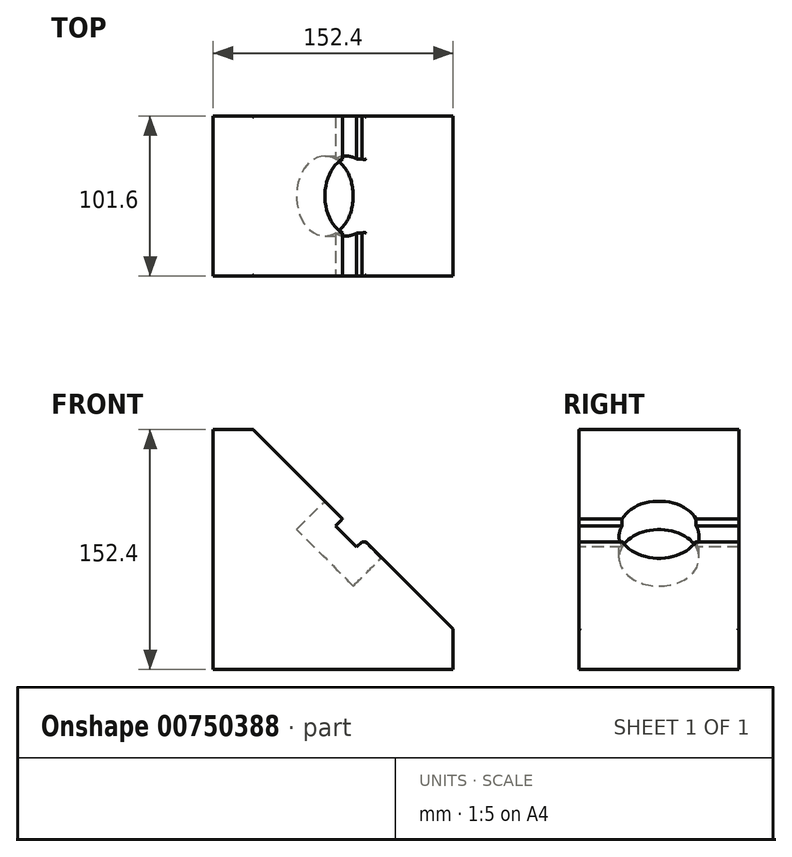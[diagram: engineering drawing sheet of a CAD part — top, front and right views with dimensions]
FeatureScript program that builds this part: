
annotation { "Feature Type Name" : "Feature", "Feature Type Description" : "" }
export const myFeature = defineFeature(function(context is Context, id is Id, definition is map)
    precondition{}
    {
        {
            var Q0;
            Q0=qCreatedBy(makeId("Front.planeOp"),FACE);
            var sketch = newSketch(context, id + "F0", { "sketchPlane" : qUnion([Q0])});
            skLineSegment(sketch, "E0", {"start": v(0, 0) * mm, "end": v(152.4, 0) * mm});
            skLineSegment(sketch, "E1", {"start": v(0, 0) * mm, "end": v(0, 152.4) * mm});
            skLineSegment(sketch, "E2", {"start": v(152.4, 0) * mm, "end": v(152.4, 25.4) * mm});
            skLineSegment(sketch, "E3", {"start": v(0, 152.4) * mm, "end": v(25.4, 152.4) * mm});
            skLineSegment(sketch, "E4", {"start": v(25.4, 152.4) * mm, "end": v(152.4, 25.4) * mm});
            skSolve(sketch);
        }
        {
            var Q0;
            Q0=makeQuery(id+"F0.imprint","IMPRINT",FACE,{"disambiguationData":[TD([[makeQuery(id+"F0.imprint","IMPRINT",EDGE,{"derivedFrom":sQuery(id+"F0.wireOp",EDGE,"E0")}),1.0]])]});
            extrude(context, id + "F1", {"entities" : qUnion([Q0]), "depth" : 50.8 * mm, "offsetDistance" : 25.4 * mm, "hasSecondDirection" : true, "secondDirectionOppositeDirection" : true, "secondDirectionDepth" : 50.8 * mm});
        }
        {
            var Q0;
            Q0=makeQuery(id+"F1.opExtrude","SWEPT_FACE",FACE,{"disambiguationData":[OSD([sQuery(id+"F0.wireOp",EDGE,"E4")])]});
            var sketch = newSketch(context, id + "F2", { "sketchPlane" : qUnion([Q0])});
            skCircle(sketch, "E5", {"center": v(0, 0) * mm, "radius": 25.4 * mm});
            skSolve(sketch);
        }
        {
            var Q0;
            Q0=makeQuery(id+"F2.imprint","IMPRINT",FACE,{"disambiguationData":[TD([[makeQuery(id+"F2.imprint","IMPRINT",EDGE,{"derivedFrom":sQuery(id+"F2.wireOp",EDGE,"E5")}),1.0]])]});
            var Q1;
            Q1=sQuery(id+"F2.wireOp",EDGE,"E5");
            extrude(context, id + "F3", {"entities" : qUnion([Q0]), "operationType" : NewBodyOperationType.REMOVE, "surfaceEntities" : qUnion([Q1]), "oppositeDirection" : true, "depth" : 25.4 * mm, "offsetDistance" : 25.4 * mm});
        }
        {
            var Q0;
            Q0=makeQuery(id+"F1.opExtrude","SWEPT_FACE",FACE,{"disambiguationData":[OSD([sQuery(id+"F0.wireOp",EDGE,"E4")])]});
            var sketch = newSketch(context, id + "F4", { "sketchPlane" : qUnion([Q0])});
            skPoint(sketch, "E6.middle", {"position": v(0, 0) * mm});
            skLineSegment(sketch, "E7.bottom", {"start": v(55.28, 9.53) * mm, "end": v(-55.28, 9.53) * mm});
            skLineSegment(sketch, "E7.top", {"start": v(55.28, -9.53) * mm, "end": v(-55.28, -9.53) * mm});
            skLineSegment(sketch, "E7.left", {"start": v(55.28, 9.53) * mm, "end": v(55.28, -9.53) * mm});
            skLineSegment(sketch, "E7.right", {"start": v(-55.28, 9.53) * mm, "end": v(-55.28, -9.53) * mm});
            skSolve(sketch);
        }
        {
            var Q0;
            Q0 = qSketchRegion(id + "F4", true);
            extrude(context, id + "F5", {"entities" : qUnion([Q0]), "operationType" : NewBodyOperationType.REMOVE, "oppositeDirection" : true, "depth" : 6.35 * mm, "offsetDistance" : 25.4 * mm});
        }
        {
            var Q0;
            {var subQ0=sQuery(id+"F0.wireOp",EDGE,"E4");var subQ1=sQuery(id+"F4.wireOp",EDGE,"E7.bottom");Q0=makeQuery(id+"F5.boolean.opBoolean","COPY",EDGE,{"disambiguationData":[TD([makeQuery(id+"F1.opExtrude","CAP_FACE",FACE,{"disambiguationData":[OSD([sQuery(id+"F0.wireOp",EDGE,"E0"),sQuery(id+"F0.wireOp",EDGE,"E1"),sQuery(id+"F0.wireOp",EDGE,"E2"),sQuery(id+"F0.wireOp",EDGE,"E3"),subQ0])],"isStart":false})])],"derivedFrom":makeQuery(id+"F5.opExtrude","CAP_EDGE",EDGE,{"disambiguationData":[OSD([subQ1])],"isStart":true})});}
            var Q1;
            {var subQ0=sQuery(id+"F0.wireOp",EDGE,"E4");var subQ1=sQuery(id+"F4.wireOp",EDGE,"E7.top");Q1=makeQuery(id+"F5.boolean.opBoolean","COPY",EDGE,{"disambiguationData":[TD([makeQuery(id+"F1.opExtrude","CAP_FACE",FACE,{"disambiguationData":[OSD([sQuery(id+"F0.wireOp",EDGE,"E0"),sQuery(id+"F0.wireOp",EDGE,"E1"),sQuery(id+"F0.wireOp",EDGE,"E2"),sQuery(id+"F0.wireOp",EDGE,"E3"),subQ0])],"isStart":false})])],"derivedFrom":makeQuery(id+"F5.opExtrude","CAP_EDGE",EDGE,{"disambiguationData":[OSD([subQ1])],"isStart":true})});}
            var Q2;
            {var subQ0=sQuery(id+"F0.wireOp",EDGE,"E4");var subQ1=sQuery(id+"F4.wireOp",EDGE,"E7.top");Q2=makeQuery(id+"F5.boolean.opBoolean","COPY",EDGE,{"disambiguationData":[TD([makeQuery(id+"F1.opExtrude","CAP_FACE",FACE,{"disambiguationData":[OSD([sQuery(id+"F0.wireOp",EDGE,"E0"),sQuery(id+"F0.wireOp",EDGE,"E1"),sQuery(id+"F0.wireOp",EDGE,"E2"),sQuery(id+"F0.wireOp",EDGE,"E3"),subQ0])],"isStart":true})])],"derivedFrom":makeQuery(id+"F5.opExtrude","CAP_EDGE",EDGE,{"disambiguationData":[OSD([subQ1])],"isStart":true})});}
            var Q3;
            {var subQ0=sQuery(id+"F0.wireOp",EDGE,"E4");var subQ1=sQuery(id+"F4.wireOp",EDGE,"E7.bottom");Q3=makeQuery(id+"F5.boolean.opBoolean","COPY",EDGE,{"disambiguationData":[TD([makeQuery(id+"F1.opExtrude","CAP_FACE",FACE,{"disambiguationData":[OSD([sQuery(id+"F0.wireOp",EDGE,"E0"),sQuery(id+"F0.wireOp",EDGE,"E1"),sQuery(id+"F0.wireOp",EDGE,"E2"),sQuery(id+"F0.wireOp",EDGE,"E3"),subQ0])],"isStart":true})])],"derivedFrom":makeQuery(id+"F5.opExtrude","CAP_EDGE",EDGE,{"disambiguationData":[OSD([subQ1])],"isStart":true})});}
            var Q4;
            {var subQ0=sQuery(id+"F2.wireOp",EDGE,"E5");Q4=makeQuery(id+"F5.boolean.opBoolean","SPLIT",EDGE,{"disambiguationData":[TD([makeQuery(id+"F5.opExtrude","SWEPT_FACE",FACE,{"disambiguationData":[OSD([sQuery(id+"F4.wireOp",EDGE,"E7.bottom")])]})])],"derivedFrom":makeQuery(id+"F3.boolean.opBoolean","COPY",EDGE,{"derivedFrom":makeQuery(id+"F3.opExtrude","CAP_EDGE",EDGE,{"disambiguationData":[OSD([subQ0])],"isStart":true})})});}
            var Q5;
            {var subQ0=sQuery(id+"F2.wireOp",EDGE,"E5");Q5=makeQuery(id+"F5.boolean.opBoolean","SPLIT",EDGE,{"disambiguationData":[TD([makeQuery(id+"F5.opExtrude","SWEPT_FACE",FACE,{"disambiguationData":[OSD([sQuery(id+"F4.wireOp",EDGE,"E7.top")])]})])],"derivedFrom":makeQuery(id+"F3.boolean.opBoolean","COPY",EDGE,{"derivedFrom":makeQuery(id+"F3.opExtrude","CAP_EDGE",EDGE,{"disambiguationData":[OSD([subQ0])],"isStart":true})})});}
            chamfer(context, id + "F6", {"entities" : qUnion([Q0, Q1, Q2, Q3, Q4, Q5]), "width" : 1.52 * mm, "tangentPropagation" : true});
        }
        {
            var Q0;
            Q0=makeQuery(id+"F1.opExtrude","SWEPT_EDGE",EDGE,{"disambiguationData":[OSD([sQuery(id+"F0.wireOp",EDGE,"E3"),sQuery(id+"F0.wireOp",EDGE,"E4")])]});
            var Q1;
            {var subQ0=sQuery(id+"F0.wireOp",EDGE,"E4");var subQ1=sQuery(id+"F0.wireOp",EDGE,"E3");Q1=makeQuery(id+"F5.boolean.opBoolean","SPLIT",EDGE,{"disambiguationData":[TD([makeQuery(id+"F1.opExtrude","SWEPT_FACE",FACE,{"disambiguationData":[OSD([subQ1])]})])],"derivedFrom":makeQuery(id+"F1.opExtrude","CAP_EDGE",EDGE,{"disambiguationData":[OSD([subQ0])],"isStart":false})});}
            var Q2;
            {var subQ0=sQuery(id+"F0.wireOp",EDGE,"E4");var subQ1=sQuery(id+"F0.wireOp",EDGE,"E3");Q2=makeQuery(id+"F5.boolean.opBoolean","SPLIT",EDGE,{"disambiguationData":[TD([makeQuery(id+"F1.opExtrude","SWEPT_FACE",FACE,{"disambiguationData":[OSD([subQ1])]})])],"derivedFrom":makeQuery(id+"F1.opExtrude","CAP_EDGE",EDGE,{"disambiguationData":[OSD([subQ0])],"isStart":true})});}
            var Q3;
            {var subQ0=sQuery(id+"F0.wireOp",EDGE,"E4");var subQ1=sQuery(id+"F0.wireOp",EDGE,"E2");Q3=makeQuery(id+"F5.boolean.opBoolean","SPLIT",EDGE,{"disambiguationData":[TD([makeQuery(id+"F1.opExtrude","SWEPT_FACE",FACE,{"disambiguationData":[OSD([subQ1])]})])],"derivedFrom":makeQuery(id+"F1.opExtrude","CAP_EDGE",EDGE,{"disambiguationData":[OSD([subQ0])],"isStart":true})});}
            var Q4;
            {var subQ0=sQuery(id+"F0.wireOp",EDGE,"E2");var subQ1=sQuery(id+"F0.wireOp",EDGE,"E4");Q4=makeQuery(id+"F5.boolean.opBoolean","SPLIT",FACE,{"disambiguationData":[TD([makeQuery(id+"F1.opExtrude","SWEPT_FACE",FACE,{"disambiguationData":[OSD([subQ0])]})])],"derivedFrom":makeQuery(id+"F1.opExtrude","SWEPT_FACE",FACE,{"disambiguationData":[OSD([subQ1])]})});}
            fillet(context, id + "F7", {"entities" : qUnion([Q0, Q1, Q2, Q3, Q4]), "radius" : 0.76 * mm, "tangentPropagation" : true, "allowEdgeOverflow" : false});
        }
    });
